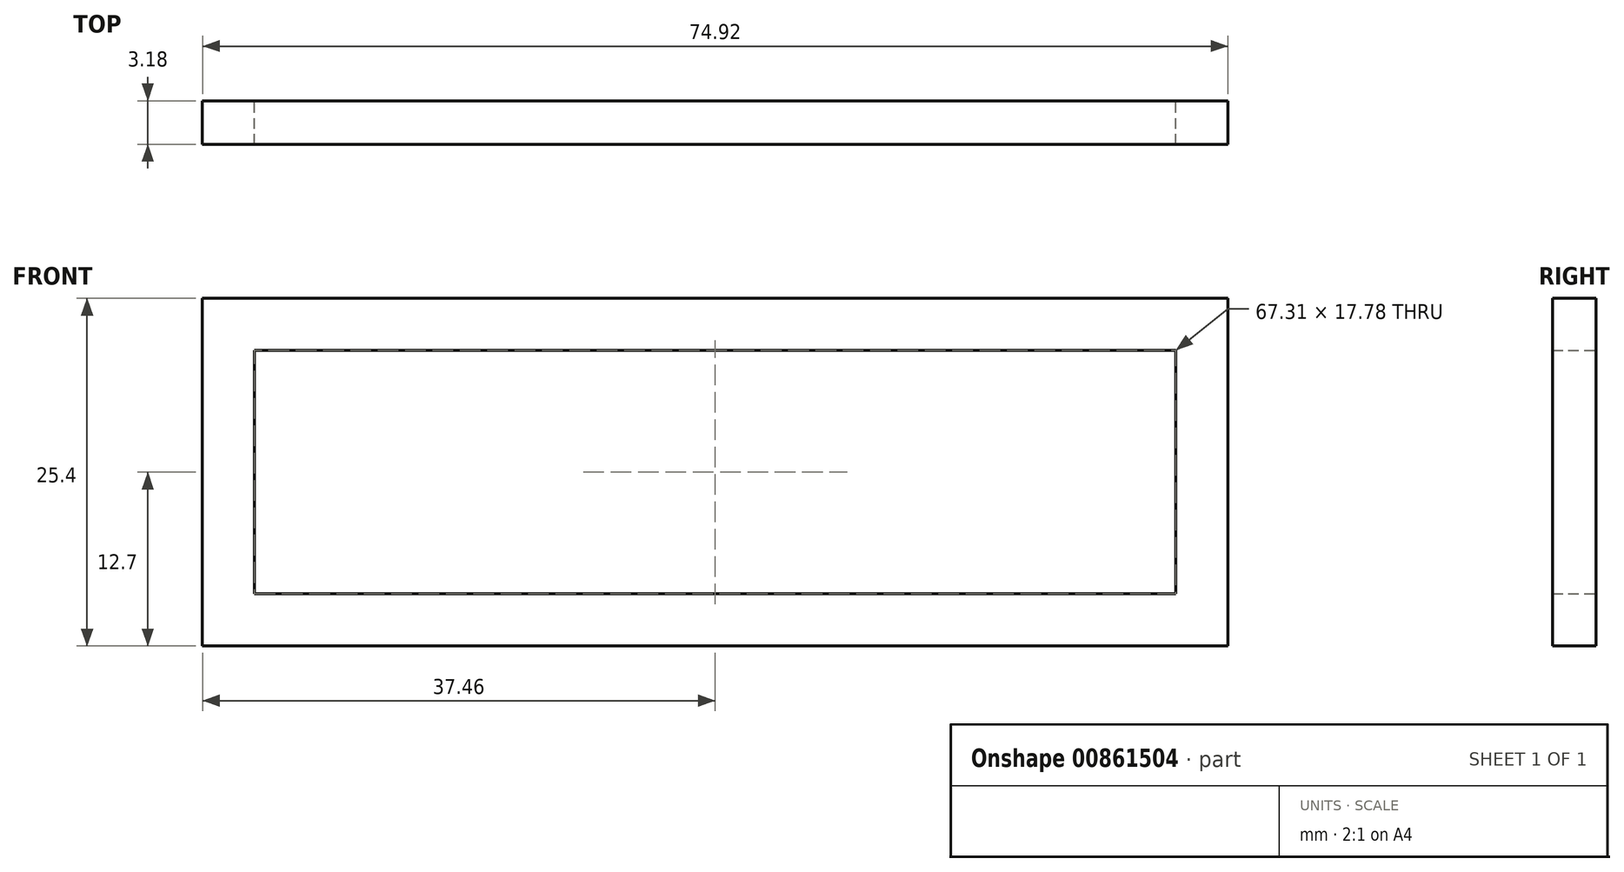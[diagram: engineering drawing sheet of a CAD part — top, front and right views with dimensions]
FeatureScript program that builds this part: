
annotation { "Feature Type Name" : "Feature", "Feature Type Description" : "" }
export const myFeature = defineFeature(function(context is Context, id is Id, definition is map)
    precondition{}
    {
        {
            var Q0;
            Q0=qCreatedBy(makeId("Front.planeOp"),FACE);
            var sketch = newSketch(context, id + "F0", { "sketchPlane" : qUnion([Q0])});
            skLineSegment(sketch, "E0.bottom", {"start": v(37.47, 12.7) * mm, "end": v(-37.47, 12.7) * mm});
            skLineSegment(sketch, "E0.top", {"start": v(37.47, -12.7) * mm, "end": v(-37.47, -12.7) * mm});
            skLineSegment(sketch, "E0.left", {"start": v(37.46, 12.7) * mm, "end": v(37.47, -12.7) * mm});
            skLineSegment(sketch, "E0.right", {"start": v(-37.47, 12.7) * mm, "end": v(-37.47, -12.7) * mm});
            skPoint(sketch, "E0.middle", {"position": v(0, 0) * mm});
            skLineSegment(sketch, "E1.bottom", {"start": v(33.66, -8.9) * mm, "end": v(-33.66, -8.9) * mm});
            skLineSegment(sketch, "E1.top", {"start": v(33.66, 8.9) * mm, "end": v(-33.66, 8.9) * mm});
            skLineSegment(sketch, "E1.left", {"start": v(33.66, -8.89) * mm, "end": v(33.66, 8.9) * mm});
            skLineSegment(sketch, "E1.right", {"start": v(-33.66, -8.9) * mm, "end": v(-33.66, 8.9) * mm});
            skSolve(sketch);
        }
        {
            var Q0;
            Q0 = qSketchRegion(id + "F0", true);
            extrude(context, id + "F1", {"entities" : qUnion([Q0]), "depth" : 3.17 * mm, "offsetDistance" : 25.4 * mm, "symmetric" : true});
        }
    });
